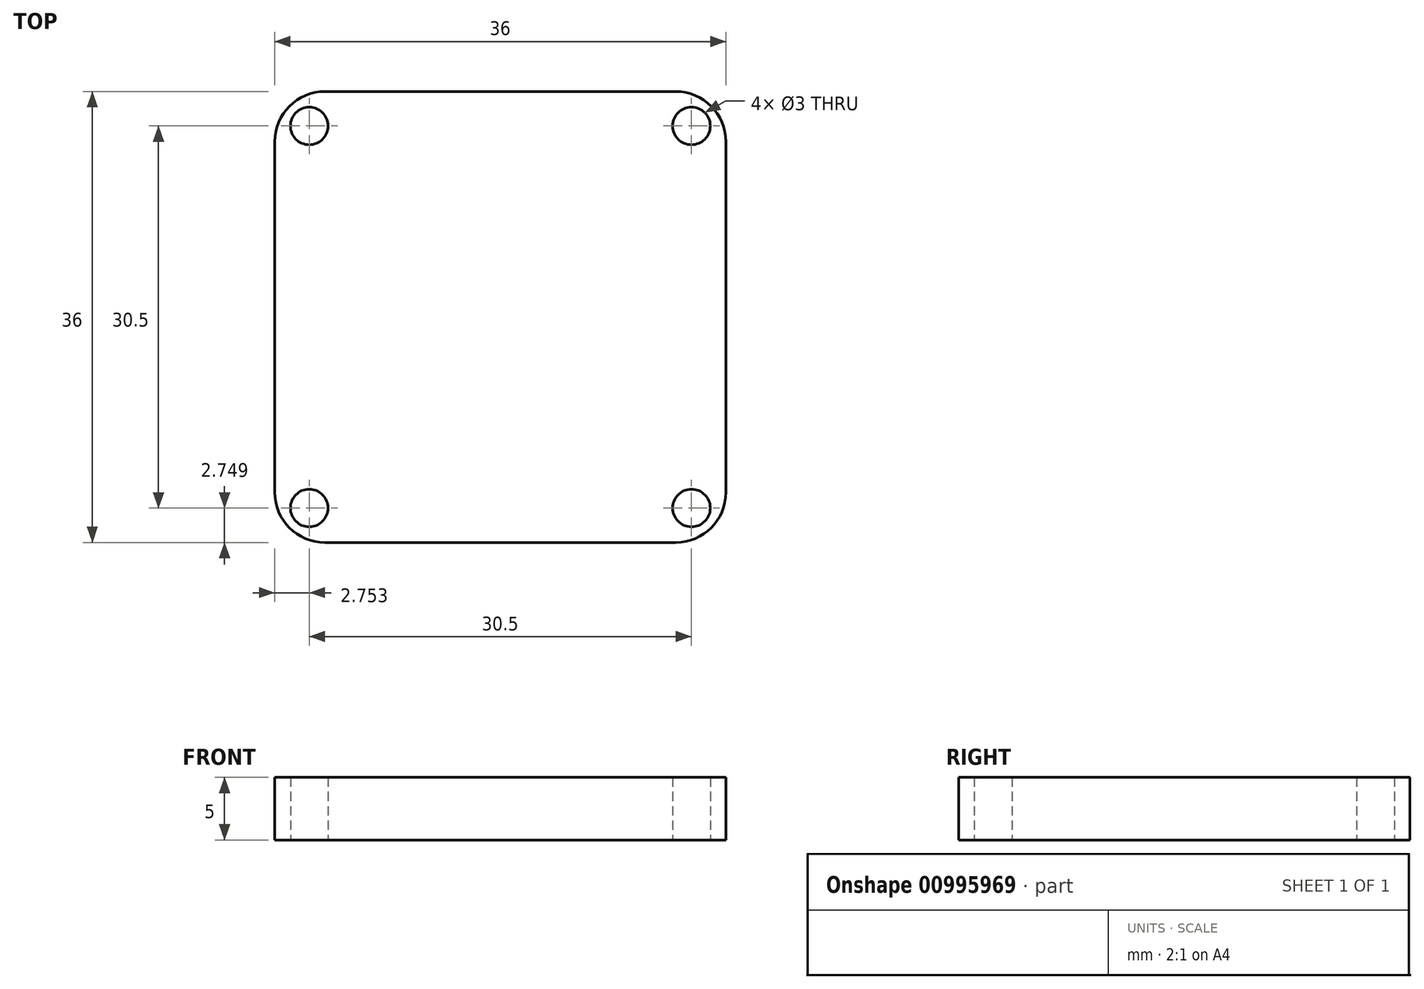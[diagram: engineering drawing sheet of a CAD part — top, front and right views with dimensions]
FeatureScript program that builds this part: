
annotation { "Feature Type Name" : "Feature", "Feature Type Description" : "" }
export const myFeature = defineFeature(function(context is Context, id is Id, definition is map)
    precondition{}
    {
        {
            var Q0;
            Q0=qCreatedBy(makeId("Top.planeOp"),FACE);
            var sketch = newSketch(context, id + "F0", { "sketchPlane" : qUnion([Q0])});
            skLineSegment(sketch, "E0.bottom", {"start": v(-21.13, 13.8) * mm, "end": v(14.87, 13.8) * mm});
            skLineSegment(sketch, "E0.top", {"start": v(-21.13, -22.2) * mm, "end": v(14.87, -22.2) * mm});
            skLineSegment(sketch, "E0.left", {"start": v(-21.13, 13.8) * mm, "end": v(-21.13, -22.2) * mm});
            skLineSegment(sketch, "E0.right", {"start": v(14.87, 13.8) * mm, "end": v(14.87, -22.2) * mm});
            skLineSegment(sketch, "E1.0", {"start": v(-18.38, 11.05) * mm, "end": v(-18.38, -19.45) * mm, "construction": true});
            skLineSegment(sketch, "E1.1", {"start": v(-18.38, 11.05) * mm, "end": v(12.12, 11.05) * mm, "construction": true});
            skLineSegment(sketch, "E1.2", {"start": v(12.12, 11.05) * mm, "end": v(12.12, -19.45) * mm, "construction": true});
            skLineSegment(sketch, "E1.3", {"start": v(-18.38, -19.45) * mm, "end": v(12.12, -19.45) * mm, "construction": true});
            skSolve(sketch);
        }
        {
            var Q0;
            Q0=makeQuery(id+"F0.imprint","IMPRINT",FACE,{"disambiguationData":[TD([[makeQuery(id+"F0.imprint","IMPRINT",EDGE,{"derivedFrom":sQuery(id+"F0.wireOp",EDGE,"E0.bottom")}),-1.0]])]});
            extrude(context, id + "F1", {"entities" : qUnion([Q0]), "depth" : 5 * mm, "offsetDistance" : 25 * mm});
        }
        {
            var Q0;
            Q0=sQuery(id+"F0.wireOp",VERTEX,"E1.2.start");
            var Q1;
            Q1=sQuery(id+"F0.wireOp",VERTEX,"E1.1.start");
            var Q2;
            Q2=sQuery(id+"F0.wireOp",VERTEX,"E1.0.end");
            var Q3;
            Q3=sQuery(id+"F0.wireOp",VERTEX,"E1.3.end");
            var Q4;
            Q4=makeQuery(id+"F1.opExtrude","SWEPT_BODY",BODY,{"disambiguationData":[OSD([sQuery(id+"F0.wireOp",EDGE,"E0.bottom"),sQuery(id+"F0.wireOp",EDGE,"E0.top"),sQuery(id+"F0.wireOp",EDGE,"E0.left"),sQuery(id+"F0.wireOp",EDGE,"E0.right")])]});
            hole(context, id + "F2", {"style" : HoleStyle.SIMPLE, "endStyle" : HoleEndStyle.THROUGH, "oppositeDirection" : true, "holeDiameter" : 3 * mm, "majorDiameter" : 5 * mm, "isTappedThrough" : true, "tappedDepth" : 12 * mm, "tapClearance" : 3, "locations" : qUnion([Q0, Q1, Q2, Q3]), "scope" : qUnion([Q4])});
        }
        {
            var Q0;
            Q0=makeQuery(id+"F1.opExtrude","SWEPT_EDGE",EDGE,{"disambiguationData":[OSD([sQuery(id+"F0.wireOp",EDGE,"E0.top"),sQuery(id+"F0.wireOp",EDGE,"E0.right")])]});
            var Q1;
            Q1=makeQuery(id+"F1.opExtrude","SWEPT_EDGE",EDGE,{"disambiguationData":[OSD([sQuery(id+"F0.wireOp",EDGE,"E0.bottom"),sQuery(id+"F0.wireOp",EDGE,"E0.right")])]});
            var Q2;
            Q2=makeQuery(id+"F1.opExtrude","SWEPT_EDGE",EDGE,{"disambiguationData":[OSD([sQuery(id+"F0.wireOp",EDGE,"E0.top"),sQuery(id+"F0.wireOp",EDGE,"E0.left")])]});
            var Q3;
            Q3=makeQuery(id+"F1.opExtrude","SWEPT_EDGE",EDGE,{"disambiguationData":[OSD([sQuery(id+"F0.wireOp",EDGE,"E0.bottom"),sQuery(id+"F0.wireOp",EDGE,"E0.left")])]});
            fillet(context, id + "F3", {"entities" : qUnion([Q0, Q1, Q2, Q3]), "radius" : 4 * mm, "tangentPropagation" : true, "allowEdgeOverflow" : false});
        }
    });
